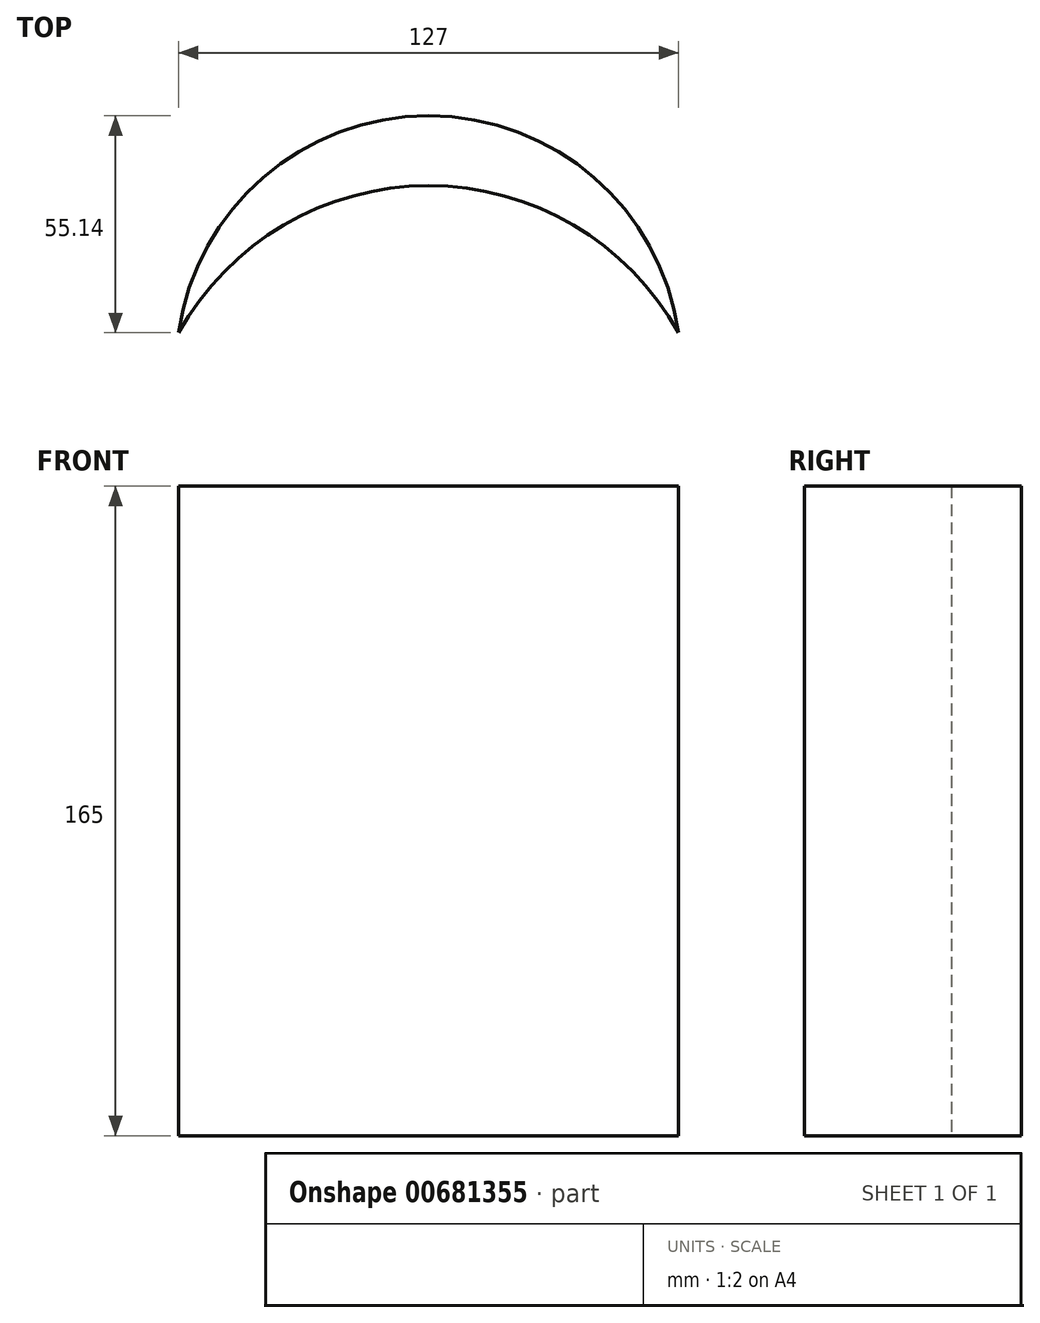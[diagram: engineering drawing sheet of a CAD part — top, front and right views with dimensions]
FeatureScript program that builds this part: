
annotation { "Feature Type Name" : "Feature", "Feature Type Description" : "" }
export const myFeature = defineFeature(function(context is Context, id is Id, definition is map)
    precondition{}
    {
        {
            var Q0;
            Q0=qCreatedBy(makeId("Top.planeOp"),FACE);
            var sketch = newSketch(context, id + "F0", { "sketchPlane" : qUnion([Q0])});
            skArc(sketch, "E0", {"start": v(66.04, 0) * mm, "mid": v(2.54, 37.36) * mm, "end": v(-60.96, 0) * mm});
            skArc(sketch, "E1", {"start": v(66.04, 0) * mm, "mid": v(2.54, 55.14) * mm, "end": v(-60.96, 0) * mm});
            skSolve(sketch);
        }
        {
            var Q0;
            Q0=makeQuery(id+"F0.imprint","IMPRINT",FACE,{"disambiguationData":[TD([[makeQuery(id+"F0.imprint","IMPRINT",EDGE,{"derivedFrom":sQuery(id+"F0.wireOp",EDGE,"E0")}),-1.0]])]});
            extrude(context, id + "F1", {"entities" : qUnion([Q0]), "endBound" : BoundingType.SYMMETRIC, "depth" : 165 * mm, "offsetDistance" : 25.4 * mm});
        }
    });
